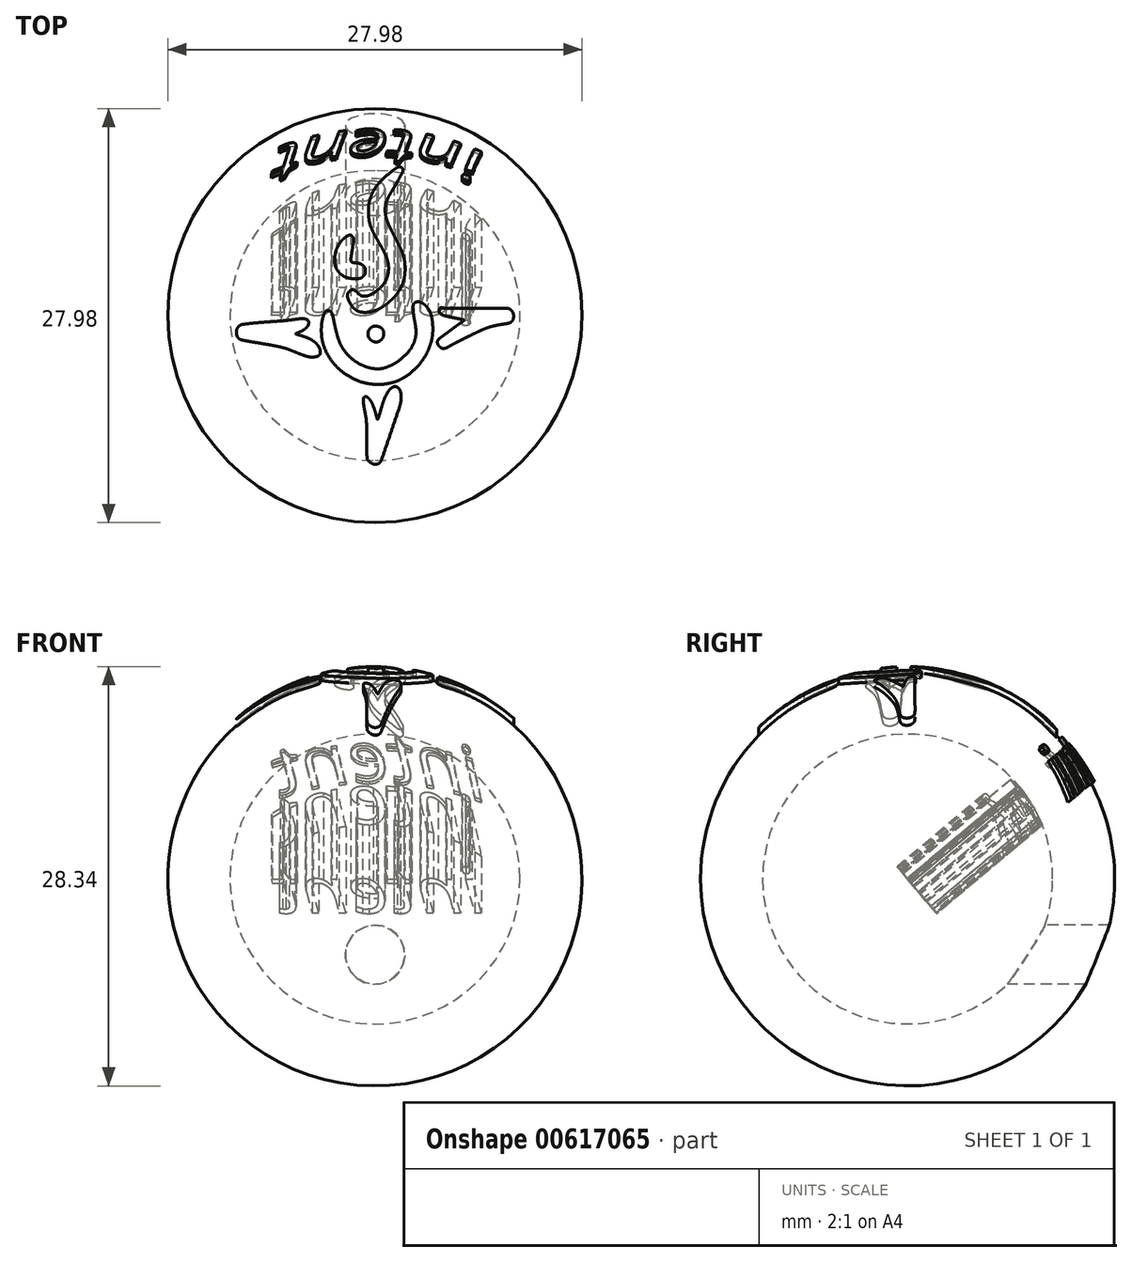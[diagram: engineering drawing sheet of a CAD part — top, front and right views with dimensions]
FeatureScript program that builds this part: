
annotation { "Feature Type Name" : "Feature", "Feature Type Description" : "" }
export const myFeature = defineFeature(function(context is Context, id is Id, definition is map)
    precondition{}
    {
        {
            var Q0;
            Q0=qCreatedBy(makeId("Top.planeOp"),FACE);
            var sketch = newSketch(context, id + "F0", { "sketchPlane" : qUnion([Q0])});
            skLineSegment(sketch, "E0", {"start": v(0, -10) * mm, "end": v(0, 10) * mm});
            skArc(sketch, "E1", {"start": v(0, 10) * mm, "mid": v(-10, 0) * mm, "end": v(0, -10) * mm});
            skSolve(sketch);
        }
        {
            var Q0;
            {var subQ0=sQuery(id+"F0.wireOp",EDGE,"E1");Q0=makeQuery(id+"F0.imprint","IMPRINT",FACE,{"disambiguationData":[TD([[makeQuery(id+"F0.imprint","IMPRINT",EDGE,{"derivedFrom":subQ0}),1.0]])]});}
            var Q1;
            Q1=sQuery(id+"F0.wireOp",EDGE,"E0");
            revolve(context, id + "F1", {"entities" : qUnion([Q0]), "axis" : qUnion([Q1]), "revolveType" : RevolveType.FULL});
        }
        {
            var Q0;
            Q0=makeQuery(id+"F1.opRevolve","SWEPT_BODY",BODY,{"disambiguationData":[OSD([sQuery(id+"F0.wireOp",EDGE,"E0"),sQuery(id+"F0.wireOp",EDGE,"E1")])]});
            var Q1;
            Q1=sQuery(id+"F0.wireOp",VERTEX,"NPe4G0ez-t7S9-9isL-QO5v-uuJu600mHcIT.center");
            var Q2;
            Q2=sQuery(id+"F0.wireOp",VERTEX,"E1.center");
            transform(context, id + "F2", {"entities" : qUnion([Q0]), "transformType" : TransformType.SCALE_UNIFORMLY, "scale" : 33.3, "scalePoint" : qUnion([Q2]), "makeCopy" : false});
        }
        {
            var Q0;
            Q0=qCreatedBy(makeId("Top.planeOp"),FACE);
            var sketch = newSketch(context, id + "F3", { "sketchPlane" : qUnion([Q0])});
            skArc(sketch, "E2", {"start": v(29.01, 233.55) * mm, "mid": v(19.13, 225.53) * mm, "end": v(9.84, 216.83) * mm});
            skArc(sketch, "E3", {"start": v(9.84, 216.83) * mm, "mid": v(3.12, 209.1) * mm, "end": v(-2.51, 200.54) * mm});
            skArc(sketch, "E4", {"start": v(-2.51, 200.54) * mm, "mid": v(-6.44, 192.13) * mm, "end": v(-9.04, 183.21) * mm});
            skArc(sketch, "E5", {"start": v(-9.04, 183.21) * mm, "mid": v(-10.44, 173.41) * mm, "end": v(-10.58, 163.51) * mm});
            skArc(sketch, "E6", {"start": v(-10.58, 163.51) * mm, "mid": v(-10.1, 157.75) * mm, "end": v(-9.24, 152.03) * mm});
            skArc(sketch, "E7", {"start": v(-9.24, 152.03) * mm, "mid": v(-8.07, 147.04) * mm, "end": v(-6.42, 142.18) * mm});
            skArc(sketch, "E8", {"start": v(-6.42, 142.18) * mm, "mid": v(-3.83, 136.15) * mm, "end": v(-0.88, 130.3) * mm});
            skArc(sketch, "E9", {"start": v(-0.88, 130.3) * mm, "mid": v(4.67, 120.25) * mm, "end": v(10.35, 110.28) * mm});
            skArc(sketch, "E10", {"start": v(10.35, 110.28) * mm, "mid": v(14.5, 102.5) * mm, "end": v(18.1, 94.45) * mm});
            skArc(sketch, "E11", {"start": v(18.1, 94.45) * mm, "mid": v(20.33, 87.78) * mm, "end": v(21.65, 80.87) * mm});
            skArc(sketch, "E12", {"start": v(21.65, 80.87) * mm, "mid": v(21.93, 74.62) * mm, "end": v(21.23, 68.4) * mm});
            skArc(sketch, "E13", {"start": v(21.23, 68.4) * mm, "mid": v(19.56, 62.07) * mm, "end": v(17.04, 56.03) * mm});
            skArc(sketch, "E14", {"start": v(17.04, 56.03) * mm, "mid": v(14.27, 51.34) * mm, "end": v(10.87, 47.1) * mm});
            skArc(sketch, "E15", {"start": v(10.87, 47.1) * mm, "mid": v(6.45, 42.75) * mm, "end": v(1.63, 38.84) * mm});
            skArc(sketch, "E16", {"start": v(1.63, 38.84) * mm, "mid": v(-3.27, 35.59) * mm, "end": v(-8.46, 32.84) * mm});
            skArc(sketch, "E17", {"start": v(-8.46, 32.84) * mm, "mid": v(-12.69, 31.4) * mm, "end": v(-17.12, 30.9) * mm});
            skArc(sketch, "E18", {"start": v(-17.12, 30.9) * mm, "mid": v(-18.57, 30.96) * mm, "end": v(-20.02, 31.11) * mm});
            skArc(sketch, "E19", {"start": v(-20.02, 31.11) * mm, "mid": v(-21.08, 31.35) * mm, "end": v(-22.08, 31.77) * mm});
            skArc(sketch, "E20", {"start": v(-22.08, 31.77) * mm, "mid": v(-23.2, 32.43) * mm, "end": v(-24.25, 33.22) * mm});
            skArc(sketch, "E21", {"start": v(-24.25, 33.22) * mm, "mid": v(-26.12, 34.84) * mm, "end": v(-27.96, 36.5) * mm});
            skArc(sketch, "E22", {"start": v(-27.96, 36.5) * mm, "mid": v(-29.65, 38.02) * mm, "end": v(-31.37, 39.52) * mm});
            skArc(sketch, "E23", {"start": v(-31.37, 39.52) * mm, "mid": v(-32.36, 40.29) * mm, "end": v(-33.42, 40.95) * mm});
            skArc(sketch, "E24", {"start": v(-33.42, 40.95) * mm, "mid": v(-34.2, 41.3) * mm, "end": v(-35.03, 41.5) * mm});
            skArc(sketch, "E25", {"start": v(-35.03, 41.5) * mm, "mid": v(-35.87, 41.54) * mm, "end": v(-36.7, 41.42) * mm});
            skArc(sketch, "E26", {"start": v(-36.7, 41.42) * mm, "mid": v(-38, 41) * mm, "end": v(-39.22, 40.4) * mm});
            skArc(sketch, "E27", {"start": v(-39.22, 40.4) * mm, "mid": v(-40.42, 39.6) * mm, "end": v(-41.52, 38.67) * mm});
            skArc(sketch, "E28", {"start": v(-41.52, 38.67) * mm, "mid": v(-42.45, 37.64) * mm, "end": v(-43.25, 36.51) * mm});
            skArc(sketch, "E29", {"start": v(-43.25, 36.51) * mm, "mid": v(-43.8, 35.42) * mm, "end": v(-44.14, 34.24) * mm});
            skArc(sketch, "E30", {"start": v(-44.14, 34.24) * mm, "mid": v(-44.33, 31.9) * mm, "end": v(-44.03, 29.59) * mm});
            skArc(sketch, "E31", {"start": v(-44.03, 29.59) * mm, "mid": v(-43.16, 26.53) * mm, "end": v(-42.02, 23.57) * mm});
            skArc(sketch, "E32", {"start": v(-42.02, 23.57) * mm, "mid": v(-40.5, 20.42) * mm, "end": v(-38.71, 17.4) * mm});
            skArc(sketch, "E33", {"start": v(-38.71, 17.4) * mm, "mid": v(-36.76, 14.69) * mm, "end": v(-34.56, 12.17) * mm});
            skArc(sketch, "E34", {"start": v(-34.56, 12.17) * mm, "mid": v(-32.5, 10.26) * mm, "end": v(-30.24, 8.58) * mm});
            skArc(sketch, "E35", {"start": v(-30.24, 8.58) * mm, "mid": v(-27.94, 7.28) * mm, "end": v(-25.49, 6.3) * mm});
            skArc(sketch, "E36", {"start": v(-25.49, 6.3) * mm, "mid": v(-22.72, 5.57) * mm, "end": v(-19.9, 5.18) * mm});
            skArc(sketch, "E37", {"start": v(-19.9, 5.18) * mm, "mid": v(-16.44, 5.03) * mm, "end": v(-12.99, 5.12) * mm});
            skArc(sketch, "E38", {"start": v(-12.99, 5.12) * mm, "mid": v(-7.73, 5.76) * mm, "end": v(-2.58, 7.01) * mm});
            skArc(sketch, "E39", {"start": v(-2.58, 7.01) * mm, "mid": v(2.77, 8.95) * mm, "end": v(7.9, 11.39) * mm});
            skArc(sketch, "E40", {"start": v(7.9, 11.39) * mm, "mid": v(13.3, 14.6) * mm, "end": v(18.4, 18.25) * mm});
            skArc(sketch, "E41", {"start": v(18.4, 18.25) * mm, "mid": v(23.75, 22.74) * mm, "end": v(28.83, 27.56) * mm});
            skArc(sketch, "E42", {"start": v(28.83, 27.56) * mm, "mid": v(33.48, 32.7) * mm, "end": v(37.66, 38.24) * mm});
            skArc(sketch, "E43", {"start": v(37.66, 38.24) * mm, "mid": v(41.04, 43.77) * mm, "end": v(43.8, 49.62) * mm});
            skArc(sketch, "E44", {"start": v(43.8, 49.62) * mm, "mid": v(45.9, 55.75) * mm, "end": v(47.34, 62.07) * mm});
            skArc(sketch, "E45", {"start": v(47.34, 62.07) * mm, "mid": v(48.2, 68.96) * mm, "end": v(48.46, 75.9) * mm});
            skArc(sketch, "E46", {"start": v(48.46, 75.9) * mm, "mid": v(48.28, 80.88) * mm, "end": v(47.83, 85.83) * mm});
            skArc(sketch, "E47", {"start": v(47.83, 85.83) * mm, "mid": v(47.14, 90.3) * mm, "end": v(46.11, 94.69) * mm});
            skArc(sketch, "E48", {"start": v(46.11, 94.69) * mm, "mid": v(44.7, 99.28) * mm, "end": v(42.96, 103.76) * mm});
            skArc(sketch, "E49", {"start": v(42.96, 103.76) * mm, "mid": v(40.56, 109.13) * mm, "end": v(37.96, 114.4) * mm});
            skArc(sketch, "E50", {"start": v(37.96, 114.4) * mm, "mid": v(32.65, 124.74) * mm, "end": v(27.37, 135.1) * mm});
            skArc(sketch, "E51", {"start": v(27.37, 135.1) * mm, "mid": v(24.73, 140.42) * mm, "end": v(22.2, 145.8) * mm});
            skArc(sketch, "E52", {"start": v(22.2, 145.8) * mm, "mid": v(20.66, 149.32) * mm, "end": v(19.27, 152.9) * mm});
            skArc(sketch, "E53", {"start": v(19.27, 152.9) * mm, "mid": v(18.3, 155.87) * mm, "end": v(17.54, 158.9) * mm});
            skArc(sketch, "E54", {"start": v(17.54, 158.9) * mm, "mid": v(16.72, 163.9) * mm, "end": v(16.36, 168.93) * mm});
            skArc(sketch, "E55", {"start": v(16.36, 168.93) * mm, "mid": v(16.52, 173.6) * mm, "end": v(17.22, 178.24) * mm});
            skArc(sketch, "E56", {"start": v(17.22, 178.24) * mm, "mid": v(18.5, 183.02) * mm, "end": v(20.27, 187.63) * mm});
            skArc(sketch, "E57", {"start": v(20.27, 187.63) * mm, "mid": v(22.83, 192.87) * mm, "end": v(25.73, 197.93) * mm});
            skArc(sketch, "E58", {"start": v(25.73, 197.93) * mm, "mid": v(28.95, 203.25) * mm, "end": v(32.1, 208.61) * mm});
            skArc(sketch, "E59", {"start": v(32.1, 208.61) * mm, "mid": v(35.38, 214.4) * mm, "end": v(38.59, 220.22) * mm});
            skArc(sketch, "E60", {"start": v(38.59, 220.22) * mm, "mid": v(41.58, 225.77) * mm, "end": v(44.55, 231.33) * mm});
            skArc(sketch, "E61", {"start": v(44.55, 231.33) * mm, "mid": v(45, 232.47) * mm, "end": v(45.14, 233.69) * mm});
            skArc(sketch, "E62", {"start": v(45.14, 233.69) * mm, "mid": v(45.05, 234.64) * mm, "end": v(44.77, 235.56) * mm});
            skArc(sketch, "E63", {"start": v(44.77, 235.56) * mm, "mid": v(44.32, 236.46) * mm, "end": v(43.72, 237.27) * mm});
            skArc(sketch, "E64", {"start": v(43.72, 237.27) * mm, "mid": v(42.97, 238) * mm, "end": v(42.1, 238.6) * mm});
            skArc(sketch, "E65", {"start": v(42.1, 238.6) * mm, "mid": v(41.14, 239.08) * mm, "end": v(40.11, 239.4) * mm});
            skArc(sketch, "E66", {"start": v(40.11, 239.4) * mm, "mid": v(39.26, 239.5) * mm, "end": v(38.42, 239.4) * mm});
            skArc(sketch, "E67", {"start": v(38.42, 239.4) * mm, "mid": v(37.38, 239.07) * mm, "end": v(36.4, 238.62) * mm});
            skArc(sketch, "E68", {"start": v(36.4, 238.62) * mm, "mid": v(34.96, 237.8) * mm, "end": v(33.58, 236.9) * mm});
            skArc(sketch, "E69", {"start": v(33.58, 236.9) * mm, "mid": v(31.29, 235.24) * mm, "end": v(29.01, 233.55) * mm});
            skArc(sketch, "E70", {"start": v(-45.92, 127.08) * mm, "mid": v(-50.13, 123.98) * mm, "end": v(-53.86, 120.31) * mm});
            skArc(sketch, "E71", {"start": v(-53.86, 120.31) * mm, "mid": v(-57.15, 116.09) * mm, "end": v(-59.87, 111.47) * mm});
            skArc(sketch, "E72", {"start": v(-59.87, 111.47) * mm, "mid": v(-62.06, 106.35) * mm, "end": v(-63.6, 101) * mm});
            skArc(sketch, "E73", {"start": v(-63.6, 101) * mm, "mid": v(-64.54, 95.27) * mm, "end": v(-64.85, 89.48) * mm});
            skArc(sketch, "E74", {"start": v(-64.85, 89.48) * mm, "mid": v(-64.72, 86.13) * mm, "end": v(-64.34, 82.8) * mm});
            skArc(sketch, "E75", {"start": v(-64.34, 82.8) * mm, "mid": v(-63.74, 79.95) * mm, "end": v(-62.82, 77.18) * mm});
            skArc(sketch, "E76", {"start": v(-62.82, 77.18) * mm, "mid": v(-61.64, 74.64) * mm, "end": v(-60.16, 72.26) * mm});
            skArc(sketch, "E77", {"start": v(-60.16, 72.26) * mm, "mid": v(-58.3, 69.89) * mm, "end": v(-56.23, 67.7) * mm});
            skArc(sketch, "E78", {"start": v(-56.23, 67.7) * mm, "mid": v(-54.01, 65.77) * mm, "end": v(-51.62, 64.06) * mm});
            skArc(sketch, "E79", {"start": v(-51.62, 64.06) * mm, "mid": v(-49.17, 62.64) * mm, "end": v(-46.6, 61.5) * mm});
            skArc(sketch, "E80", {"start": v(-46.6, 61.5) * mm, "mid": v(-43.73, 60.56) * mm, "end": v(-40.8, 59.9) * mm});
            skArc(sketch, "E81", {"start": v(-40.8, 59.9) * mm, "mid": v(-37.34, 59.42) * mm, "end": v(-33.86, 59.16) * mm});
            skArc(sketch, "E82", {"start": v(-33.86, 59.16) * mm, "mid": v(-30.5, 59.1) * mm, "end": v(-27.13, 59.26) * mm});
            skArc(sketch, "E83", {"start": v(-27.13, 59.26) * mm, "mid": v(-24.75, 59.62) * mm, "end": v(-22.46, 60.36) * mm});
            skArc(sketch, "E84", {"start": v(-22.46, 60.36) * mm, "mid": v(-20.66, 61.32) * mm, "end": v(-19.1, 62.63) * mm});
            skArc(sketch, "E85", {"start": v(-19.1, 62.63) * mm, "mid": v(-17.66, 64.36) * mm, "end": v(-16.5, 66.28) * mm});
            skArc(sketch, "E86", {"start": v(-16.5, 66.28) * mm, "mid": v(-15.4, 69.6) * mm, "end": v(-15.24, 73.08) * mm});
            skArc(sketch, "E87", {"start": v(-15.24, 73.08) * mm, "mid": v(-16.08, 76.33) * mm, "end": v(-17.88, 79.16) * mm});
            skArc(sketch, "E88", {"start": v(-17.88, 79.16) * mm, "mid": v(-20.75, 81.68) * mm, "end": v(-24.17, 83.38) * mm});
            skArc(sketch, "E89", {"start": v(-24.17, 83.38) * mm, "mid": v(-28.48, 84.49) * mm, "end": v(-32.91, 84.88) * mm});
            skArc(sketch, "E90", {"start": v(-32.91, 84.88) * mm, "mid": v(-34.86, 85.1) * mm, "end": v(-36.73, 85.7) * mm});
            skArc(sketch, "E91", {"start": v(-36.73, 85.7) * mm, "mid": v(-37.9, 86.6) * mm, "end": v(-38.52, 87.91) * mm});
            skArc(sketch, "E92", {"start": v(-38.52, 87.91) * mm, "mid": v(-38.8, 90.23) * mm, "end": v(-38.7, 92.56) * mm});
            skArc(sketch, "E93", {"start": v(-38.7, 92.56) * mm, "mid": v(-37.86, 98.3) * mm, "end": v(-36.95, 104.03) * mm});
            skArc(sketch, "E94", {"start": v(-36.95, 104.03) * mm, "mid": v(-35.78, 111.04) * mm, "end": v(-34.64, 118.06) * mm});
            skArc(sketch, "E95", {"start": v(-34.64, 118.06) * mm, "mid": v(-34.36, 120.3) * mm, "end": v(-34.22, 122.54) * mm});
            skArc(sketch, "E96", {"start": v(-34.22, 122.54) * mm, "mid": v(-34.32, 123.85) * mm, "end": v(-34.7, 125.11) * mm});
            skArc(sketch, "E97", {"start": v(-34.7, 125.11) * mm, "mid": v(-35.37, 126.33) * mm, "end": v(-36.26, 127.4) * mm});
            skArc(sketch, "E98", {"start": v(-36.26, 127.4) * mm, "mid": v(-37.31, 128.36) * mm, "end": v(-38.46, 129.21) * mm});
            skArc(sketch, "E99", {"start": v(-38.46, 129.21) * mm, "mid": v(-39.3, 129.61) * mm, "end": v(-40.24, 129.73) * mm});
            skArc(sketch, "E100", {"start": v(-40.24, 129.73) * mm, "mid": v(-41.31, 129.57) * mm, "end": v(-42.32, 129.17) * mm});
            skArc(sketch, "E101", {"start": v(-42.32, 129.17) * mm, "mid": v(-44.14, 128.16) * mm, "end": v(-45.92, 127.08) * mm});
            skArc(sketch, "E102", {"start": v(65.46, 21.4) * mm, "mid": v(64.85, 21.12) * mm, "end": v(64.26, 20.79) * mm});
            skArc(sketch, "E103", {"start": v(64.26, 20.79) * mm, "mid": v(63.68, 20.42) * mm, "end": v(63.13, 20) * mm});
            skArc(sketch, "E104", {"start": v(63.13, 20) * mm, "mid": v(62.68, 19.6) * mm, "end": v(62.25, 19.18) * mm});
            skArc(sketch, "E105", {"start": v(62.25, 19.18) * mm, "mid": v(61.98, 18.83) * mm, "end": v(61.79, 18.44) * mm});
            skArc(sketch, "E106", {"start": v(61.79, 18.44) * mm, "mid": v(61.29, 16.67) * mm, "end": v(61.1, 14.84) * mm});
            skArc(sketch, "E107", {"start": v(61.1, 14.84) * mm, "mid": v(61.15, 11.63) * mm, "end": v(61.3, 8.43) * mm});
            skArc(sketch, "E108", {"start": v(61.3, 8.43) * mm, "mid": v(61.65, 4.5) * mm, "end": v(62.14, 0.6) * mm});
            skArc(sketch, "E109", {"start": v(62.14, 0.6) * mm, "mid": v(62.82, -3.76) * mm, "end": v(63.62, -8.1) * mm});
            skArc(sketch, "E110", {"start": v(63.62, -8.1) * mm, "mid": v(64.53, -12.99) * mm, "end": v(65.32, -17.9) * mm});
            skArc(sketch, "E111", {"start": v(65.32, -17.9) * mm, "mid": v(65.76, -21.56) * mm, "end": v(65.99, -25.23) * mm});
            skArc(sketch, "E112", {"start": v(65.99, -25.23) * mm, "mid": v(65.98, -28.33) * mm, "end": v(65.74, -31.42) * mm});
            skArc(sketch, "E113", {"start": v(65.74, -31.42) * mm, "mid": v(65.29, -34.5) * mm, "end": v(64.6, -37.55) * mm});
            skArc(sketch, "E114", {"start": v(64.6, -37.55) * mm, "mid": v(61.01, -47.26) * mm, "end": v(55.57, -56.05) * mm});
            skArc(sketch, "E115", {"start": v(55.57, -56.05) * mm, "mid": v(47.83, -64.8) * mm, "end": v(38.95, -72.38) * mm});
            skArc(sketch, "E116", {"start": v(38.95, -72.38) * mm, "mid": v(29.3, -78.52) * mm, "end": v(18.86, -83.23) * mm});
            skArc(sketch, "E117", {"start": v(18.86, -83.23) * mm, "mid": v(9.39, -85.53) * mm, "end": v(-0.36, -85.64) * mm});
            skArc(sketch, "E118", {"start": v(-0.36, -85.64) * mm, "mid": v(-9.01, -84.12) * mm, "end": v(-17.37, -81.43) * mm});
            skArc(sketch, "E119", {"start": v(-17.37, -81.43) * mm, "mid": v(-25.6, -77.52) * mm, "end": v(-33.3, -72.63) * mm});
            skArc(sketch, "E120", {"start": v(-33.3, -72.63) * mm, "mid": v(-40.35, -66.8) * mm, "end": v(-46.63, -60.13) * mm});
            skArc(sketch, "E121", {"start": v(-46.63, -60.13) * mm, "mid": v(-51.86, -52.93) * mm, "end": v(-56.07, -45.1) * mm});
            skArc(sketch, "E122", {"start": v(-56.07, -45.1) * mm, "mid": v(-57.45, -41.85) * mm, "end": v(-58.65, -38.55) * mm});
            skArc(sketch, "E123", {"start": v(-58.65, -38.55) * mm, "mid": v(-59.98, -34.42) * mm, "end": v(-61.19, -30.25) * mm});
            skArc(sketch, "E124", {"start": v(-61.19, -30.25) * mm, "mid": v(-62.51, -25.22) * mm, "end": v(-63.72, -20.17) * mm});
            skArc(sketch, "E125", {"start": v(-63.72, -20.17) * mm, "mid": v(-65.05, -14.14) * mm, "end": v(-66.29, -8.1) * mm});
            skArc(sketch, "E126", {"start": v(-66.29, -8.1) * mm, "mid": v(-67.21, -3.72) * mm, "end": v(-68.25, 0.62) * mm});
            skArc(sketch, "E127", {"start": v(-68.25, 0.62) * mm, "mid": v(-68.99, 2.87) * mm, "end": v(-70.04, 4.98) * mm});
            skArc(sketch, "E128", {"start": v(-70.04, 4.98) * mm, "mid": v(-71.06, 6.23) * mm, "end": v(-72.4, 7.13) * mm});
            skArc(sketch, "E129", {"start": v(-72.4, 7.13) * mm, "mid": v(-74.06, 7.7) * mm, "end": v(-75.82, 7.9) * mm});
            skArc(sketch, "E130", {"start": v(-75.82, 7.9) * mm, "mid": v(-77.16, 7.74) * mm, "end": v(-78.43, 7.27) * mm});
            skArc(sketch, "E131", {"start": v(-78.43, 7.27) * mm, "mid": v(-79.54, 6.5) * mm, "end": v(-80.43, 5.5) * mm});
            skArc(sketch, "E132", {"start": v(-80.43, 5.5) * mm, "mid": v(-81.4, 3.84) * mm, "end": v(-82.13, 2.07) * mm});
            skArc(sketch, "E133", {"start": v(-82.13, 2.07) * mm, "mid": v(-83.1, -1) * mm, "end": v(-83.99, -4.1) * mm});
            skArc(sketch, "E134", {"start": v(-83.99, -4.1) * mm, "mid": v(-85.1, -9.01) * mm, "end": v(-85.83, -14) * mm});
            skArc(sketch, "E135", {"start": v(-85.83, -14) * mm, "mid": v(-86.25, -19.46) * mm, "end": v(-86.34, -24.93) * mm});
            skArc(sketch, "E136", {"start": v(-86.34, -24.93) * mm, "mid": v(-86.1, -30.38) * mm, "end": v(-85.54, -35.8) * mm});
            skArc(sketch, "E137", {"start": v(-85.54, -35.8) * mm, "mid": v(-84.67, -40.74) * mm, "end": v(-83.43, -45.6) * mm});
            skArc(sketch, "E138", {"start": v(-83.43, -45.6) * mm, "mid": v(-77.13, -61.14) * mm, "end": v(-68, -75.2) * mm});
            skArc(sketch, "E139", {"start": v(-68, -75.2) * mm, "mid": v(-56.22, -87.58) * mm, "end": v(-42.42, -97.64) * mm});
            skArc(sketch, "E140", {"start": v(-42.42, -97.64) * mm, "mid": v(-27.05, -105.06) * mm, "end": v(-10.6, -109.6) * mm});
            skArc(sketch, "E141", {"start": v(-10.6, -109.6) * mm, "mid": v(6.07, -111) * mm, "end": v(22.7, -109.2) * mm});
            skArc(sketch, "E142", {"start": v(22.7, -109.2) * mm, "mid": v(34.18, -105.87) * mm, "end": v(45, -100.8) * mm});
            skArc(sketch, "E143", {"start": v(45, -100.8) * mm, "mid": v(55.53, -93.83) * mm, "end": v(65.05, -85.53) * mm});
            skArc(sketch, "E144", {"start": v(65.05, -85.53) * mm, "mid": v(73.6, -75.81) * mm, "end": v(80.84, -65.07) * mm});
            skArc(sketch, "E145", {"start": v(80.84, -65.07) * mm, "mid": v(86.55, -53.59) * mm, "end": v(90.67, -41.45) * mm});
            skArc(sketch, "E146", {"start": v(90.67, -41.45) * mm, "mid": v(91.87, -36) * mm, "end": v(92.6, -30.49) * mm});
            skArc(sketch, "E147", {"start": v(92.6, -30.49) * mm, "mid": v(92.96, -24.25) * mm, "end": v(92.94, -18) * mm});
            skArc(sketch, "E148", {"start": v(92.94, -18) * mm, "mid": v(92.53, -11.87) * mm, "end": v(91.75, -5.78) * mm});
            skArc(sketch, "E149", {"start": v(91.75, -5.78) * mm, "mid": v(90.67, -0.67) * mm, "end": v(89.09, 4.31) * mm});
            skArc(sketch, "E150", {"start": v(89.09, 4.31) * mm, "mid": v(87.2, 8.44) * mm, "end": v(84.75, 12.25) * mm});
            skArc(sketch, "E151", {"start": v(84.75, 12.25) * mm, "mid": v(81.83, 15.6) * mm, "end": v(78.44, 18.46) * mm});
            skArc(sketch, "E152", {"start": v(78.44, 18.46) * mm, "mid": v(75.14, 20.43) * mm, "end": v(71.54, 21.78) * mm});
            skArc(sketch, "E153", {"start": v(71.54, 21.78) * mm, "mid": v(68.47, 22.1) * mm, "end": v(65.46, 21.4) * mm});
            skArc(sketch, "E154", {"start": v(103.85, 10.27) * mm, "mid": v(103.2, 8.18) * mm, "end": v(103.3, 5.98) * mm});
            skArc(sketch, "E155", {"start": v(103.3, 5.98) * mm, "mid": v(104.13, 4.02) * mm, "end": v(105.62, 2.5) * mm});
            skArc(sketch, "E156", {"start": v(105.62, 2.5) * mm, "mid": v(108.58, 0.82) * mm, "end": v(111.77, -0.35) * mm});
            skArc(sketch, "E157", {"start": v(111.77, -0.35) * mm, "mid": v(117.43, -1.78) * mm, "end": v(123.14, -3) * mm});
            skArc(sketch, "E158", {"start": v(123.14, -3) * mm, "mid": v(125.34, -3.44) * mm, "end": v(127.55, -3.88) * mm});
            skArc(sketch, "E159", {"start": v(127.55, -3.88) * mm, "mid": v(129.83, -4.33) * mm, "end": v(132.11, -4.78) * mm});
            skArc(sketch, "E160", {"start": v(132.11, -4.78) * mm, "mid": v(134.16, -5.19) * mm, "end": v(136.2, -5.6) * mm});
            skArc(sketch, "E161", {"start": v(136.2, -5.6) * mm, "mid": v(137.57, -5.88) * mm, "end": v(138.94, -6.16) * mm});
            skLineSegment(sketch, "E162", {"start": v(138.94, -6.16) * mm, "end": v(144.24, -7.26) * mm});
            skLineSegment(sketch, "E163", {"start": v(144.24, -7.26) * mm, "end": v(138.6, -11.21) * mm});
            skArc(sketch, "E164", {"start": v(138.6, -11.21) * mm, "mid": v(137.18, -12.21) * mm, "end": v(135.77, -13.23) * mm});
            skArc(sketch, "E165", {"start": v(135.77, -13.23) * mm, "mid": v(133.77, -14.68) * mm, "end": v(131.77, -16.14) * mm});
            skArc(sketch, "E166", {"start": v(131.77, -16.14) * mm, "mid": v(129.58, -17.75) * mm, "end": v(127.4, -19.37) * mm});
            skArc(sketch, "E167", {"start": v(127.4, -19.37) * mm, "mid": v(125.35, -20.9) * mm, "end": v(123.3, -22.45) * mm});
            skArc(sketch, "E168", {"start": v(123.3, -22.45) * mm, "mid": v(121.22, -24) * mm, "end": v(119.15, -25.54) * mm});
            skArc(sketch, "E169", {"start": v(119.15, -25.54) * mm, "mid": v(116.91, -27.18) * mm, "end": v(114.67, -28.8) * mm});
            skArc(sketch, "E170", {"start": v(114.67, -28.8) * mm, "mid": v(112.6, -30.3) * mm, "end": v(110.53, -31.78) * mm});
            skArc(sketch, "E171", {"start": v(110.53, -31.78) * mm, "mid": v(109.02, -32.83) * mm, "end": v(107.5, -33.87) * mm});
            skArc(sketch, "E172", {"start": v(107.5, -33.87) * mm, "mid": v(104.91, -35.81) * mm, "end": v(102.52, -38) * mm});
            skArc(sketch, "E173", {"start": v(102.52, -38) * mm, "mid": v(101.18, -39.8) * mm, "end": v(100.4, -41.9) * mm});
            skArc(sketch, "E174", {"start": v(100.4, -41.9) * mm, "mid": v(100.3, -43.94) * mm, "end": v(100.88, -45.9) * mm});
            skArc(sketch, "E175", {"start": v(100.88, -45.9) * mm, "mid": v(102.25, -48.24) * mm, "end": v(103.94, -50.34) * mm});
            skArc(sketch, "E176", {"start": v(103.94, -50.34) * mm, "mid": v(105.3, -51.53) * mm, "end": v(106.85, -52.43) * mm});
            skArc(sketch, "E177", {"start": v(106.85, -52.43) * mm, "mid": v(108.5, -52.96) * mm, "end": v(110.22, -53.1) * mm});
            skArc(sketch, "E178", {"start": v(110.22, -53.1) * mm, "mid": v(112.2, -52.89) * mm, "end": v(114.12, -52.31) * mm});
            skArc(sketch, "E179", {"start": v(114.12, -52.31) * mm, "mid": v(116.4, -51.27) * mm, "end": v(118.59, -50.02) * mm});
            skArc(sketch, "E180", {"start": v(118.59, -50.02) * mm, "mid": v(120.15, -49.08) * mm, "end": v(121.76, -48.19) * mm});
            skArc(sketch, "E181", {"start": v(121.76, -48.19) * mm, "mid": v(125.82, -46.06) * mm, "end": v(129.89, -43.95) * mm});
            skArc(sketch, "E182", {"start": v(129.89, -43.95) * mm, "mid": v(134.76, -41.44) * mm, "end": v(139.64, -38.96) * mm});
            skArc(sketch, "E183", {"start": v(139.64, -38.96) * mm, "mid": v(144.95, -36.29) * mm, "end": v(150.27, -33.64) * mm});
            skArc(sketch, "E184", {"start": v(150.27, -33.64) * mm, "mid": v(159.77, -29) * mm, "end": v(169.33, -24.46) * mm});
            skArc(sketch, "E185", {"start": v(169.33, -24.46) * mm, "mid": v(175.2, -21.89) * mm, "end": v(181.2, -19.6) * mm});
            skArc(sketch, "E186", {"start": v(181.2, -19.6) * mm, "mid": v(186.48, -17.91) * mm, "end": v(191.84, -16.56) * mm});
            skArc(sketch, "E187", {"start": v(191.84, -16.56) * mm, "mid": v(198.67, -15.2) * mm, "end": v(205.54, -14.04) * mm});
            skArc(sketch, "E188", {"start": v(205.54, -14.04) * mm, "mid": v(208.79, -13.53) * mm, "end": v(212.03, -12.98) * mm});
            skArc(sketch, "E189", {"start": v(212.03, -12.98) * mm, "mid": v(213.87, -12.6) * mm, "end": v(215.7, -12.11) * mm});
            skArc(sketch, "E190", {"start": v(215.7, -12.11) * mm, "mid": v(216.92, -11.68) * mm, "end": v(218.09, -11.13) * mm});
            skArc(sketch, "E191", {"start": v(218.09, -11.13) * mm, "mid": v(219.06, -10.5) * mm, "end": v(219.93, -9.76) * mm});
            skArc(sketch, "E192", {"start": v(219.93, -9.76) * mm, "mid": v(221.11, -8.3) * mm, "end": v(221.97, -6.62) * mm});
            skArc(sketch, "E193", {"start": v(221.97, -6.62) * mm, "mid": v(222.6, -4.57) * mm, "end": v(222.93, -2.44) * mm});
            skArc(sketch, "E194", {"start": v(222.93, -2.44) * mm, "mid": v(222.96, -0.25) * mm, "end": v(222.7, 1.92) * mm});
            skArc(sketch, "E195", {"start": v(222.7, 1.92) * mm, "mid": v(222.14, 3.83) * mm, "end": v(221.24, 5.6) * mm});
            skArc(sketch, "E196", {"start": v(221.24, 5.6) * mm, "mid": v(219.73, 7.65) * mm, "end": v(217.92, 9.44) * mm});
            skArc(sketch, "E197", {"start": v(217.92, 9.44) * mm, "mid": v(216.13, 10.6) * mm, "end": v(214.1, 11.29) * mm});
            skArc(sketch, "E198", {"start": v(214.1, 11.29) * mm, "mid": v(210.86, 11.76) * mm, "end": v(207.59, 11.92) * mm});
            skArc(sketch, "E199", {"start": v(207.59, 11.92) * mm, "mid": v(198.73, 11.88) * mm, "end": v(189.88, 11.78) * mm});
            skArc(sketch, "E200", {"start": v(189.88, 11.78) * mm, "mid": v(175.63, 11.6) * mm, "end": v(161.38, 11.47) * mm});
            skArc(sketch, "E201", {"start": v(161.38, 11.47) * mm, "mid": v(148.64, 11.43) * mm, "end": v(135.9, 11.47) * mm});
            skArc(sketch, "E202", {"start": v(135.9, 11.47) * mm, "mid": v(125.01, 11.56) * mm, "end": v(114.12, 11.68) * mm});
            skArc(sketch, "E203", {"start": v(114.12, 11.68) * mm, "mid": v(111.53, 11.85) * mm, "end": v(108.98, 12.3) * mm});
            skArc(sketch, "E204", {"start": v(108.98, 12.3) * mm, "mid": v(107.88, 12.53) * mm, "end": v(106.78, 12.7) * mm});
            skArc(sketch, "E205", {"start": v(106.78, 12.7) * mm, "mid": v(106.2, 12.72) * mm, "end": v(105.65, 12.58) * mm});
            skArc(sketch, "E206", {"start": v(105.65, 12.58) * mm, "mid": v(105.18, 12.3) * mm, "end": v(104.81, 11.9) * mm});
            skArc(sketch, "E207", {"start": v(104.81, 11.9) * mm, "mid": v(104.3, 11.1) * mm, "end": v(103.85, 10.27) * mm});
            skArc(sketch, "E208", {"start": v(-131.36, -6.65) * mm, "mid": v(-133.6, -7) * mm, "end": v(-135.83, -7.27) * mm});
            skArc(sketch, "E209", {"start": v(-135.83, -7.27) * mm, "mid": v(-139.72, -7.68) * mm, "end": v(-143.62, -8.06) * mm});
            skArc(sketch, "E210", {"start": v(-143.62, -8.06) * mm, "mid": v(-148.14, -8.47) * mm, "end": v(-152.66, -8.86) * mm});
            skArc(sketch, "E211", {"start": v(-152.66, -8.86) * mm, "mid": v(-157.26, -9.22) * mm, "end": v(-161.86, -9.55) * mm});
            skArc(sketch, "E212", {"start": v(-161.86, -9.55) * mm, "mid": v(-173.2, -10.37) * mm, "end": v(-184.55, -11.25) * mm});
            skArc(sketch, "E213", {"start": v(-184.55, -11.25) * mm, "mid": v(-192.69, -11.96) * mm, "end": v(-200.81, -12.79) * mm});
            skArc(sketch, "E214", {"start": v(-200.81, -12.79) * mm, "mid": v(-206.72, -13.48) * mm, "end": v(-212.61, -14.24) * mm});
            skArc(sketch, "E215", {"start": v(-212.61, -14.24) * mm, "mid": v(-214.78, -14.73) * mm, "end": v(-216.83, -15.58) * mm});
            skArc(sketch, "E216", {"start": v(-216.83, -15.58) * mm, "mid": v(-219.48, -17.53) * mm, "end": v(-221.38, -20.22) * mm});
            skArc(sketch, "E217", {"start": v(-221.38, -20.22) * mm, "mid": v(-222.6, -23.66) * mm, "end": v(-222.98, -27.29) * mm});
            skArc(sketch, "E218", {"start": v(-222.98, -27.29) * mm, "mid": v(-222.51, -30.87) * mm, "end": v(-221.21, -34.25) * mm});
            skArc(sketch, "E219", {"start": v(-221.21, -34.25) * mm, "mid": v(-219.25, -36.82) * mm, "end": v(-216.57, -38.61) * mm});
            skArc(sketch, "E220", {"start": v(-216.57, -38.61) * mm, "mid": v(-215.48, -39.03) * mm, "end": v(-214.35, -39.34) * mm});
            skArc(sketch, "E221", {"start": v(-214.35, -39.34) * mm, "mid": v(-211.03, -40.03) * mm, "end": v(-207.7, -40.7) * mm});
            skArc(sketch, "E222", {"start": v(-207.7, -40.7) * mm, "mid": v(-203.7, -41.46) * mm, "end": v(-199.71, -42.18) * mm});
            skArc(sketch, "E223", {"start": v(-199.71, -42.18) * mm, "mid": v(-195.29, -42.94) * mm, "end": v(-190.86, -43.67) * mm});
            skArc(sketch, "E224", {"start": v(-190.86, -43.67) * mm, "mid": v(-179.98, -45.46) * mm, "end": v(-169.1, -47.31) * mm});
            skArc(sketch, "E225", {"start": v(-169.1, -47.31) * mm, "mid": v(-161.88, -48.66) * mm, "end": v(-154.68, -50.16) * mm});
            skArc(sketch, "E226", {"start": v(-154.68, -50.16) * mm, "mid": v(-149.45, -51.4) * mm, "end": v(-144.25, -52.8) * mm});
            skArc(sketch, "E227", {"start": v(-144.25, -52.8) * mm, "mid": v(-140.08, -54.14) * mm, "end": v(-135.99, -55.72) * mm});
            skArc(sketch, "E228", {"start": v(-135.99, -55.72) * mm, "mid": v(-130.47, -58) * mm, "end": v(-124.93, -60.26) * mm});
            skArc(sketch, "E229", {"start": v(-124.93, -60.26) * mm, "mid": v(-120.71, -61.9) * mm, "end": v(-116.47, -63.47) * mm});
            skArc(sketch, "E230", {"start": v(-116.47, -63.47) * mm, "mid": v(-113.25, -64.59) * mm, "end": v(-110, -65.63) * mm});
            skArc(sketch, "E231", {"start": v(-110, -65.63) * mm, "mid": v(-107.83, -66.2) * mm, "end": v(-105.61, -66.62) * mm});
            skArc(sketch, "E232", {"start": v(-105.61, -66.62) * mm, "mid": v(-103.25, -66.88) * mm, "end": v(-100.88, -66.95) * mm});
            skArc(sketch, "E233", {"start": v(-100.88, -66.95) * mm, "mid": v(-98.54, -66.85) * mm, "end": v(-96.2, -66.56) * mm});
            skArc(sketch, "E234", {"start": v(-96.2, -66.56) * mm, "mid": v(-94.2, -66.14) * mm, "end": v(-92.24, -65.56) * mm});
            skArc(sketch, "E235", {"start": v(-92.24, -65.56) * mm, "mid": v(-90.93, -64.93) * mm, "end": v(-89.79, -64.02) * mm});
            skArc(sketch, "E236", {"start": v(-89.79, -64.02) * mm, "mid": v(-88.55, -62.26) * mm, "end": v(-88, -60.17) * mm});
            skArc(sketch, "E237", {"start": v(-88, -60.17) * mm, "mid": v(-88.02, -57.48) * mm, "end": v(-88.54, -54.84) * mm});
            skArc(sketch, "E238", {"start": v(-88.54, -54.84) * mm, "mid": v(-89.66, -51.83) * mm, "end": v(-91.23, -49.03) * mm});
            skArc(sketch, "E239", {"start": v(-91.23, -49.03) * mm, "mid": v(-93.28, -46.32) * mm, "end": v(-95.66, -43.89) * mm});
            skArc(sketch, "E240", {"start": v(-95.66, -43.89) * mm, "mid": v(-97.72, -42.15) * mm, "end": v(-99.9, -40.55) * mm});
            skArc(sketch, "E241", {"start": v(-99.9, -40.55) * mm, "mid": v(-102.15, -39.12) * mm, "end": v(-104.5, -37.84) * mm});
            skArc(sketch, "E242", {"start": v(-104.5, -37.84) * mm, "mid": v(-107.34, -36.51) * mm, "end": v(-110.26, -35.34) * mm});
            skArc(sketch, "E243", {"start": v(-110.26, -35.34) * mm, "mid": v(-114.24, -33.92) * mm, "end": v(-118.25, -32.59) * mm});
            skLineSegment(sketch, "E244", {"start": v(-118.25, -32.59) * mm, "end": v(-128.14, -29.44) * mm});
            skLineSegment(sketch, "E245", {"start": v(-128.14, -29.44) * mm, "end": v(-122.48, -27.14) * mm});
            skArc(sketch, "E246", {"start": v(-122.48, -27.14) * mm, "mid": v(-119.78, -25.96) * mm, "end": v(-117.15, -24.64) * mm});
            skArc(sketch, "E247", {"start": v(-117.15, -24.64) * mm, "mid": v(-114.93, -23.33) * mm, "end": v(-112.83, -21.85) * mm});
            skArc(sketch, "E248", {"start": v(-112.83, -21.85) * mm, "mid": v(-111.13, -20.42) * mm, "end": v(-109.57, -18.83) * mm});
            skArc(sketch, "E249", {"start": v(-109.57, -18.83) * mm, "mid": v(-108.4, -17.3) * mm, "end": v(-107.44, -15.62) * mm});
            skArc(sketch, "E250", {"start": v(-107.44, -15.62) * mm, "mid": v(-106.65, -12.83) * mm, "end": v(-106.8, -9.93) * mm});
            skArc(sketch, "E251", {"start": v(-106.8, -9.93) * mm, "mid": v(-107.92, -7.7) * mm, "end": v(-109.97, -6.27) * mm});
            skArc(sketch, "E252", {"start": v(-109.97, -6.27) * mm, "mid": v(-113.9, -5.25) * mm, "end": v(-117.95, -5.09) * mm});
            skArc(sketch, "E253", {"start": v(-117.95, -5.09) * mm, "mid": v(-124.68, -5.7) * mm, "end": v(-131.36, -6.65) * mm});
            skArc(sketch, "E254", {"start": v(-6.77, -19.67) * mm, "mid": v(-9.2, -22.4) * mm, "end": v(-10.77, -25.7) * mm});
            skArc(sketch, "E255", {"start": v(-10.77, -25.7) * mm, "mid": v(-11.35, -29.33) * mm, "end": v(-10.89, -32.97) * mm});
            skArc(sketch, "E256", {"start": v(-10.89, -32.97) * mm, "mid": v(-9.42, -36.37) * mm, "end": v(-7.06, -39.22) * mm});
            skArc(sketch, "E257", {"start": v(-7.06, -39.22) * mm, "mid": v(-4, -41.32) * mm, "end": v(-0.49, -42.5) * mm});
            skArc(sketch, "E258", {"start": v(-0.49, -42.5) * mm, "mid": v(2.99, -42.62) * mm, "end": v(6.33, -41.7) * mm});
            skArc(sketch, "E259", {"start": v(6.33, -41.7) * mm, "mid": v(9.37, -39.8) * mm, "end": v(11.78, -37.15) * mm});
            skArc(sketch, "E260", {"start": v(11.78, -37.15) * mm, "mid": v(13.43, -33.86) * mm, "end": v(14.16, -30.26) * mm});
            skArc(sketch, "E261", {"start": v(14.16, -30.26) * mm, "mid": v(13.9, -26.62) * mm, "end": v(12.68, -23.18) * mm});
            skArc(sketch, "E262", {"start": v(12.68, -23.18) * mm, "mid": v(11.21, -21.09) * mm, "end": v(9.23, -19.47) * mm});
            skArc(sketch, "E263", {"start": v(9.23, -19.47) * mm, "mid": v(6.62, -18.2) * mm, "end": v(3.8, -17.4) * mm});
            skArc(sketch, "E264", {"start": v(3.8, -17.4) * mm, "mid": v(0.87, -17.15) * mm, "end": v(-2.06, -17.43) * mm});
            skArc(sketch, "E265", {"start": v(-2.06, -17.43) * mm, "mid": v(-4.56, -18.25) * mm, "end": v(-6.77, -19.67) * mm});
            skArc(sketch, "E266", {"start": v(27.49, -116.02) * mm, "mid": v(24.94, -117.92) * mm, "end": v(22.78, -120.24) * mm});
            skArc(sketch, "E267", {"start": v(22.78, -120.24) * mm, "mid": v(20.4, -123.6) * mm, "end": v(18.33, -127.14) * mm});
            skArc(sketch, "E268", {"start": v(18.33, -127.14) * mm, "mid": v(16.08, -131.78) * mm, "end": v(14.16, -136.56) * mm});
            skArc(sketch, "E269", {"start": v(14.16, -136.56) * mm, "mid": v(12.1, -142.55) * mm, "end": v(10.27, -148.62) * mm});
            skArc(sketch, "E270", {"start": v(10.27, -148.62) * mm, "mid": v(8.7, -154.13) * mm, "end": v(7.12, -159.63) * mm});
            skArc(sketch, "E271", {"start": v(7.12, -159.63) * mm, "mid": v(6.33, -162.23) * mm, "end": v(5.48, -164.8) * mm});
            skArc(sketch, "E272", {"start": v(5.48, -164.8) * mm, "mid": v(5.01, -166) * mm, "end": v(4.46, -167.15) * mm});
            skArc(sketch, "E273", {"start": v(4.46, -167.15) * mm, "mid": v(4.15, -167.32) * mm, "end": v(3.87, -167.1) * mm});
            skArc(sketch, "E274", {"start": v(3.87, -167.1) * mm, "mid": v(3.71, -166.6) * mm, "end": v(3.56, -166.1) * mm});
            skArc(sketch, "E275", {"start": v(3.56, -166.1) * mm, "mid": v(3.15, -164.68) * mm, "end": v(2.74, -163.27) * mm});
            skArc(sketch, "E276", {"start": v(2.74, -163.27) * mm, "mid": v(2.25, -161.58) * mm, "end": v(1.76, -159.89) * mm});
            skArc(sketch, "E277", {"start": v(1.76, -159.89) * mm, "mid": v(1.23, -158.03) * mm, "end": v(0.7, -156.17) * mm});
            skArc(sketch, "E278", {"start": v(0.7, -156.17) * mm, "mid": v(-1.17, -150.27) * mm, "end": v(-3.35, -144.48) * mm});
            skArc(sketch, "E279", {"start": v(-3.35, -144.48) * mm, "mid": v(-5.42, -140.1) * mm, "end": v(-7.98, -135.98) * mm});
            skArc(sketch, "E280", {"start": v(-7.98, -135.98) * mm, "mid": v(-10.1, -133.45) * mm, "end": v(-12.64, -131.33) * mm});
            skArc(sketch, "E281", {"start": v(-12.64, -131.33) * mm, "mid": v(-14.72, -130.62) * mm, "end": v(-16.86, -131.1) * mm});
            skArc(sketch, "E282", {"start": v(-16.86, -131.1) * mm, "mid": v(-17.88, -131.97) * mm, "end": v(-18.44, -133.2) * mm});
            skArc(sketch, "E283", {"start": v(-18.44, -133.2) * mm, "mid": v(-18.75, -135.34) * mm, "end": v(-18.81, -137.5) * mm});
            skArc(sketch, "E284", {"start": v(-18.81, -137.5) * mm, "mid": v(-18.6, -140.93) * mm, "end": v(-18.15, -144.33) * mm});
            skArc(sketch, "E285", {"start": v(-18.15, -144.33) * mm, "mid": v(-17.2, -149.77) * mm, "end": v(-16.15, -155.19) * mm});
            skArc(sketch, "E286", {"start": v(-16.15, -155.19) * mm, "mid": v(-15.31, -159.57) * mm, "end": v(-14.58, -163.98) * mm});
            skArc(sketch, "E287", {"start": v(-14.58, -163.98) * mm, "mid": v(-14.12, -167.49) * mm, "end": v(-13.82, -171.02) * mm});
            skArc(sketch, "E288", {"start": v(-13.82, -171.02) * mm, "mid": v(-13.6, -175.56) * mm, "end": v(-13.5, -180.1) * mm});
            skArc(sketch, "E289", {"start": v(-13.5, -180.1) * mm, "mid": v(-13.43, -189.6) * mm, "end": v(-13.4, -199.1) * mm});
            skArc(sketch, "E290", {"start": v(-13.4, -199.1) * mm, "mid": v(-13.37, -206.13) * mm, "end": v(-13.32, -213.17) * mm});
            skArc(sketch, "E291", {"start": v(-13.32, -213.17) * mm, "mid": v(-13.24, -217.98) * mm, "end": v(-13.1, -222.78) * mm});
            skArc(sketch, "E292", {"start": v(-13.1, -222.78) * mm, "mid": v(-12.95, -226.25) * mm, "end": v(-12.77, -229.7) * mm});
            skArc(sketch, "E293", {"start": v(-12.77, -229.7) * mm, "mid": v(-12.6, -230.68) * mm, "end": v(-12.2, -231.6) * mm});
            skArc(sketch, "E294", {"start": v(-12.2, -231.6) * mm, "mid": v(-11.4, -232.81) * mm, "end": v(-10.49, -233.94) * mm});
            skArc(sketch, "E295", {"start": v(-10.49, -233.94) * mm, "mid": v(-9.39, -235.05) * mm, "end": v(-8.2, -236.07) * mm});
            skArc(sketch, "E296", {"start": v(-8.2, -236.07) * mm, "mid": v(-6.9, -237) * mm, "end": v(-5.53, -237.81) * mm});
            skArc(sketch, "E297", {"start": v(-5.53, -237.81) * mm, "mid": v(-4.14, -238.48) * mm, "end": v(-2.7, -239.02) * mm});
            skArc(sketch, "E298", {"start": v(-2.7, -239.02) * mm, "mid": v(-1.05, -239.4) * mm, "end": v(0.64, -239.5) * mm});
            skArc(sketch, "E299", {"start": v(0.64, -239.5) * mm, "mid": v(2.4, -239.33) * mm, "end": v(4.13, -238.91) * mm});
            skArc(sketch, "E300", {"start": v(4.13, -238.91) * mm, "mid": v(5.7, -238.27) * mm, "end": v(7.14, -237.4) * mm});
            skArc(sketch, "E301", {"start": v(7.14, -237.4) * mm, "mid": v(8.23, -236.44) * mm, "end": v(9.06, -235.24) * mm});
            skArc(sketch, "E302", {"start": v(9.06, -235.24) * mm, "mid": v(10.25, -232.78) * mm, "end": v(11.23, -230.24) * mm});
            skArc(sketch, "E303", {"start": v(11.23, -230.24) * mm, "mid": v(18.28, -209.56) * mm, "end": v(25.31, -188.88) * mm});
            skArc(sketch, "E304", {"start": v(25.31, -188.88) * mm, "mid": v(32.2, -168.57) * mm, "end": v(39.07, -148.26) * mm});
            skArc(sketch, "E305", {"start": v(39.07, -148.26) * mm, "mid": v(40.17, -144.7) * mm, "end": v(41.05, -141.07) * mm});
            skArc(sketch, "E306", {"start": v(41.05, -141.07) * mm, "mid": v(41.76, -136.98) * mm, "end": v(42.13, -132.84) * mm});
            skArc(sketch, "E307", {"start": v(42.13, -132.84) * mm, "mid": v(42.1, -129.09) * mm, "end": v(41.67, -125.36) * mm});
            skArc(sketch, "E308", {"start": v(41.67, -125.36) * mm, "mid": v(40.95, -122.35) * mm, "end": v(39.84, -119.46) * mm});
            skArc(sketch, "E309", {"start": v(39.84, -119.46) * mm, "mid": v(38.55, -117.5) * mm, "end": v(36.74, -116) * mm});
            skArc(sketch, "E310", {"start": v(36.74, -116) * mm, "mid": v(35.45, -115.26) * mm, "end": v(34.1, -114.62) * mm});
            skArc(sketch, "E311", {"start": v(34.1, -114.62) * mm, "mid": v(33.14, -114.32) * mm, "end": v(32.13, -114.22) * mm});
            skArc(sketch, "E312", {"start": v(32.13, -114.22) * mm, "mid": v(31.12, -114.32) * mm, "end": v(30.15, -114.64) * mm});
            skArc(sketch, "E313", {"start": v(30.15, -114.64) * mm, "mid": v(28.8, -115.28) * mm, "end": v(27.49, -116.02) * mm});
            skSolve(sketch);
        }
        {
            var Q0;
            Q0=qSketchRegion(id+"F3",true);
            var Q1;
            Q1=sQuery(id+"F3.wireOp",EDGE,"c928f899-12af-4b01-b412-b3b7da3d830f");
            var Q2;
            Q2=sQuery(id+"F3.wireOp",EDGE,"b69f99c7-a6d0-4d1b-8752-9e82ab4c99ec");
            extrude(context, id + "F4", {"entities" : qUnion([Q0]), "operationType" : NewBodyOperationType.ADD, "surfaceEntities" : qUnion([Q1, Q2]), "depth" : 350 * mm});
        }
        {
            var Q0;
            Q0=makeQuery(id+"F4.opExtrude","SWEPT_BODY",BODY,{"disambiguationData":[OSD([sQuery(id+"F3.wireOp",EDGE,"15c6da4e-992d-4824-9d20-70d2d6be9970"),sQuery(id+"F3.wireOp",EDGE,"268c69ec-46be-456f-85eb-69decc32fe39"),sQuery(id+"F3.wireOp",EDGE,"1d386307-6059-4203-bca6-0c1cec3c82e1"),sQuery(id+"F3.wireOp",EDGE,"7d7c66d2-f869-427f-806b-ad436cacd60e"),sQuery(id+"F3.wireOp",EDGE,"1db91850-860e-493f-a3af-7a0f3f1512ae"),sQuery(id+"F3.wireOp",EDGE,"2c65f23b-9f03-4f6f-ab37-de452af29e3c"),sQuery(id+"F3.wireOp",EDGE,"ba006cbc-bbd7-44d9-84cc-9cde0967c280"),sQuery(id+"F3.wireOp",EDGE,"ae950208-c781-4a25-8fcf-ffe59b9085ff"),sQuery(id+"F3.wireOp",EDGE,"3cce0944-c62d-4831-9b9d-d1a418d328b4"),sQuery(id+"F3.wireOp",EDGE,"9edc5e7d-16c0-40c4-98ad-6b91d5df0e78"),sQuery(id+"F3.wireOp",EDGE,"aa452f44-44a2-4c64-bff5-a2a639df00db"),sQuery(id+"F3.wireOp",EDGE,"16259f99-ce20-4b7b-81e1-fa0909c03eb4"),sQuery(id+"F3.wireOp",EDGE,"79895566-a943-429d-b257-d76af3645bdf"),sQuery(id+"F3.wireOp",EDGE,"a85490ef-f17e-45c8-b92b-28215162778a"),sQuery(id+"F3.wireOp",EDGE,"322f1036-a6fd-4992-ab69-5919540af7a6"),sQuery(id+"F3.wireOp",EDGE,"0a87ff38-4ab4-4140-b3c3-2d7501d9f3b1"),sQuery(id+"F3.wireOp",EDGE,"a6e7bdf2-ef3e-49d4-9b3c-e34f5a41e0c4"),sQuery(id+"F3.wireOp",EDGE,"3e588790-576f-47c1-9730-f5e27fa1e8f9"),sQuery(id+"F3.wireOp",EDGE,"ce3739ef-15fd-4754-ad9c-ccf511a9a8fb"),sQuery(id+"F3.wireOp",EDGE,"201134a3-66f3-4a3f-aa9b-76948966efc0"),sQuery(id+"F3.wireOp",EDGE,"65b511ea-0759-428d-8070-88e1f521d8ea"),sQuery(id+"F3.wireOp",EDGE,"c37cddb6-5cf8-4891-aff4-7191a72080b9"),sQuery(id+"F3.wireOp",EDGE,"52a43dbd-e952-43e1-be3d-d70e107260e6"),sQuery(id+"F3.wireOp",EDGE,"08c1271f-f5c3-4f26-be27-7f5e21217dff"),sQuery(id+"F3.wireOp",EDGE,"59a09f58-0503-4180-962a-e04db21f0da8"),sQuery(id+"F3.wireOp",EDGE,"e56a4626-e956-42c3-bb5d-cd9dae1ca801"),sQuery(id+"F3.wireOp",EDGE,"5ff5d55f-af90-49eb-8040-353101557de8"),sQuery(id+"F3.wireOp",EDGE,"0ed7430b-e164-4f56-8af9-4534524aa7c0"),sQuery(id+"F3.wireOp",EDGE,"b5610a6e-b6bb-43e3-9a8d-d3d7c5f0098b"),sQuery(id+"F3.wireOp",EDGE,"1d417af8-88ad-47c2-a4e2-6fec82bd6695"),sQuery(id+"F3.wireOp",EDGE,"778ae99a-956a-4ddb-8078-d9bc57f9fc8e"),sQuery(id+"F3.wireOp",EDGE,"5b19af09-f144-446e-9dfa-8766819c9efd"),sQuery(id+"F3.wireOp",EDGE,"028339f6-0475-4a57-af8d-550e32ad7466"),sQuery(id+"F3.wireOp",EDGE,"d5ae35b6-d210-433a-92c8-e92622696872"),sQuery(id+"F3.wireOp",EDGE,"16a2e606-2caa-4876-9ffa-8f08c4ff3a37"),sQuery(id+"F3.wireOp",EDGE,"5b90b144-be56-4de7-a9dd-c1e0336acbe3"),sQuery(id+"F3.wireOp",EDGE,"5912d126-c5fc-41e4-bfb8-b4fefc52ca72"),sQuery(id+"F3.wireOp",EDGE,"2e96ce95-bd3e-4f27-a7f8-b62cf5efe954"),sQuery(id+"F3.wireOp",EDGE,"ecb4e259-1207-4dd0-bc3c-87c6506cc3a5"),sQuery(id+"F3.wireOp",EDGE,"105fb72e-4d79-4204-af2f-b3b26f5eb8d1"),sQuery(id+"F3.wireOp",EDGE,"fa59b598-df54-48c6-bb8f-c5f7618c69d0"),sQuery(id+"F3.wireOp",EDGE,"a6beef0d-f124-47ac-b957-e6cd3057a354"),sQuery(id+"F3.wireOp",EDGE,"7c3eaf53-dcb7-43b1-ad18-80ff953eb59e"),sQuery(id+"F3.wireOp",EDGE,"281fe206-104f-408f-94b6-be79f12604c9")])]});
            var Q1;
            Q1=makeQuery(id+"F4.opExtrude","SWEPT_BODY",BODY,{"disambiguationData":[OSD([sQuery(id+"F3.wireOp",EDGE,"58f6206a-5554-41d4-8cf7-6e0b4724a469"),sQuery(id+"F3.wireOp",EDGE,"85dabe77-b6aa-43d5-a519-64383616f71e"),sQuery(id+"F3.wireOp",EDGE,"4b679fe6-9e11-497d-b8fd-14ca14e49ddd"),sQuery(id+"F3.wireOp",EDGE,"51de25f6-d59e-4805-a327-1fd7e38869c8"),sQuery(id+"F3.wireOp",EDGE,"d47977fb-70d3-4df8-bc35-66fcc0e556e0"),sQuery(id+"F3.wireOp",EDGE,"235006b0-8f14-4ca2-82f0-f96b6b8c4766"),sQuery(id+"F3.wireOp",EDGE,"0fc7acd6-1c1d-47a8-ba12-62eb658d35ca"),sQuery(id+"F3.wireOp",EDGE,"883fa5e3-ca4c-4ce6-a249-4debf538fe24"),sQuery(id+"F3.wireOp",EDGE,"1da09ed1-22d9-43a1-a655-8acff5d61309"),sQuery(id+"F3.wireOp",EDGE,"32654a82-a09a-444f-bf73-45f818f0f235"),sQuery(id+"F3.wireOp",EDGE,"a398fd80-a0a9-4724-ba0e-1a7a000baa92"),sQuery(id+"F3.wireOp",EDGE,"f39f97c8-53f5-4046-9905-b28daecd4f10"),sQuery(id+"F3.wireOp",EDGE,"2484d883-0ec2-4c7d-9023-165ebbef226c"),sQuery(id+"F3.wireOp",EDGE,"f026d96f-3d32-4113-a1c9-3545f5cdbe4a"),sQuery(id+"F3.wireOp",EDGE,"974fee18-719e-4620-aace-d3676da2011b"),sQuery(id+"F3.wireOp",EDGE,"0c5766d2-a026-45af-bffd-0d1f783d5157"),sQuery(id+"F3.wireOp",EDGE,"5da13fee-9c04-45d8-805f-c7a03dde2383"),sQuery(id+"F3.wireOp",EDGE,"dbea32a3-85bd-4957-aef2-b6fe64a02f6b"),sQuery(id+"F3.wireOp",EDGE,"fba134ea-bf40-4191-ad8f-cc6b2b040a97"),sQuery(id+"F3.wireOp",EDGE,"0c19e200-7cd5-4fcb-83ed-261bd7936bc7"),sQuery(id+"F3.wireOp",EDGE,"246b843b-ea86-44e5-9cb9-335e6677b61d"),sQuery(id+"F3.wireOp",EDGE,"c1b3c9bc-1eb4-4c9b-99c8-0cebed89395a"),sQuery(id+"F3.wireOp",EDGE,"f93eebc3-1447-4029-8362-91325193ac2b"),sQuery(id+"F3.wireOp",EDGE,"bf86b12d-53a9-4c19-abaa-b1e658933ceb"),sQuery(id+"F3.wireOp",EDGE,"89646a71-1a60-4e14-b80a-74fb601d0855"),sQuery(id+"F3.wireOp",EDGE,"7b03dcde-0a52-4f3c-80e9-110d1d805e93"),sQuery(id+"F3.wireOp",EDGE,"83e8d1f3-8820-485b-8b6d-3ecd79124883"),sQuery(id+"F3.wireOp",EDGE,"ec7b56eb-ca95-44fd-a774-e9b7f9d3f50d"),sQuery(id+"F3.wireOp",EDGE,"31861aa6-cfd1-43ce-a7c5-bacfb7e2a30f"),sQuery(id+"F3.wireOp",EDGE,"fa3de647-1dd9-4141-982b-74ae8d07851d"),sQuery(id+"F3.wireOp",EDGE,"75d7c1c5-761c-4178-bfd4-4f469045899b"),sQuery(id+"F3.wireOp",EDGE,"4b3d7518-bd5d-4ecc-b2c5-d8dd665de4f4"),sQuery(id+"F3.wireOp",EDGE,"3be2682d-01bd-4f31-9cde-9df16a01e4a9"),sQuery(id+"F3.wireOp",EDGE,"72d3c7a9-2794-46eb-9b0d-6c526cc1b9a3"),sQuery(id+"F3.wireOp",EDGE,"0137e336-6b26-4f8d-b9ad-47ce1aa9eb31"),sQuery(id+"F3.wireOp",EDGE,"96000e4a-2d86-4b9f-af7d-a1c875cc048c"),sQuery(id+"F3.wireOp",EDGE,"139c5a79-9c0f-4e15-b57f-4c09662495a3"),sQuery(id+"F3.wireOp",EDGE,"8ea04d8b-b3da-46bb-9742-d8cba6b23bda"),sQuery(id+"F3.wireOp",EDGE,"b352b580-467e-481c-88ac-6217b8462947"),sQuery(id+"F3.wireOp",EDGE,"2503a493-1722-4539-8d54-7329fc0b116a"),sQuery(id+"F3.wireOp",EDGE,"a0615e06-0a48-4c65-8818-f0f693937022"),sQuery(id+"F3.wireOp",EDGE,"08389002-1ce8-438a-b5a4-698ca33590c2"),sQuery(id+"F3.wireOp",EDGE,"1756e4aa-c30a-461e-962c-81ee35d31e55"),sQuery(id+"F3.wireOp",EDGE,"5f84c249-07ea-4efb-9be3-ca494937f772"),sQuery(id+"F3.wireOp",EDGE,"cbefd041-b54f-4587-87b6-437b2290d1fc"),sQuery(id+"F3.wireOp",EDGE,"d44f58d4-f1a7-4aec-b016-8e7f1e498aeb"),sQuery(id+"F3.wireOp",EDGE,"0a5be90b-7545-44ea-9f2d-c726a5a2121c"),sQuery(id+"F3.wireOp",EDGE,"0cfaa442-d102-4580-8ef6-489f2aa1e6b3")])]});
            var Q2;
            Q2=makeQuery(id+"F4.opExtrude","SWEPT_BODY",BODY,{"disambiguationData":[OSD([sQuery(id+"F3.wireOp",EDGE,"9cc7aec6-4d94-4577-ab6c-32f5aa316238"),sQuery(id+"F3.wireOp",EDGE,"5ab2d840-4a32-405a-8c4b-a8126e3e1bc1"),sQuery(id+"F3.wireOp",EDGE,"56de48b4-9620-4637-8196-310e2641530f"),sQuery(id+"F3.wireOp",EDGE,"55327826-e64b-4830-85f2-3f22d36f43b5"),sQuery(id+"F3.wireOp",EDGE,"0245b46f-a639-4a95-8ca3-1568736ceed2"),sQuery(id+"F3.wireOp",EDGE,"9bd8a002-6ca7-4c84-8984-a620eefad103"),sQuery(id+"F3.wireOp",EDGE,"d4736c5e-da0b-46a0-ba9d-17ae07bb2b66"),sQuery(id+"F3.wireOp",EDGE,"125695b8-77e6-4e99-8f78-5f8fae1a0c71"),sQuery(id+"F3.wireOp",EDGE,"c9f25b10-a495-4684-8f25-8f255fabab6e"),sQuery(id+"F3.wireOp",EDGE,"0dbee67a-2ab6-4abb-ae16-0fe64d623848"),sQuery(id+"F3.wireOp",EDGE,"92c08d8e-ed2e-41a3-9c1a-b5ddaf8a0bf1"),sQuery(id+"F3.wireOp",EDGE,"00fabb15-0c1e-492e-85c1-17390e5b12bc"),sQuery(id+"F3.wireOp",EDGE,"065a9352-dddb-4e3f-b02a-444c867b75fe"),sQuery(id+"F3.wireOp",EDGE,"ef206bb6-e4f2-4189-9fc7-a7823c329ad6"),sQuery(id+"F3.wireOp",EDGE,"7199cbbe-c9bf-4cb9-b928-2ff8a84eb09e"),sQuery(id+"F3.wireOp",EDGE,"17bf9ed1-b881-4f74-816d-3511b6b328c7"),sQuery(id+"F3.wireOp",EDGE,"e5b615d0-4193-495d-b285-bd69ae30f000"),sQuery(id+"F3.wireOp",EDGE,"cfeaf62f-6be1-426b-9732-01e1a667be7e"),sQuery(id+"F3.wireOp",EDGE,"ac56344b-5ee6-4fa5-8e47-65b2a4ea3a01"),sQuery(id+"F3.wireOp",EDGE,"45b5fa53-15fd-43a0-91b0-943cc3286fc9")])]});
            var Q3;
            Q3=makeQuery(id+"F4.opExtrude","SWEPT_BODY",BODY,{"disambiguationData":[OSD([sQuery(id+"F3.wireOp",EDGE,"7bdfe37d-9957-4663-8239-5490fd3220d9"),sQuery(id+"F3.wireOp",EDGE,"6a91314f-c002-4565-bbf8-bb9f29165fb8"),sQuery(id+"F3.wireOp",EDGE,"b69f99c7-a6d0-4d1b-8752-9e82ab4c99ec"),sQuery(id+"F3.wireOp",EDGE,"c928f899-12af-4b01-b412-b3b7da3d830f"),sQuery(id+"F3.wireOp",EDGE,"ffa58721-cdd5-406d-be26-d96f7a050df4"),sQuery(id+"F3.wireOp",EDGE,"02fc7fb8-293b-44ff-ab78-63506d0aedb9"),sQuery(id+"F3.wireOp",EDGE,"147fb6cb-2565-4fb5-9280-6afbf9eef36b"),sQuery(id+"F3.wireOp",EDGE,"2cee3704-4124-415a-b391-31af1cf305d7"),sQuery(id+"F3.wireOp",EDGE,"32b2fb71-03c8-4978-9d95-2b5aaf044d0d"),sQuery(id+"F3.wireOp",EDGE,"e5d05796-7d6c-4350-8a4e-d55f5ade2f77"),sQuery(id+"F3.wireOp",EDGE,"77b1164c-8dd4-4680-b616-ac151a422eb2"),sQuery(id+"F3.wireOp",EDGE,"ec0798b8-0fbb-49ea-9766-39d2ee0936b0"),sQuery(id+"F3.wireOp",EDGE,"c4af6478-2a03-47a6-862f-c0c71886b8a3"),sQuery(id+"F3.wireOp",EDGE,"1912a38f-fa28-45c6-ab33-84cac2787056"),sQuery(id+"F3.wireOp",EDGE,"5d79fa95-f66d-4d2b-923b-4d54735f1fbd"),sQuery(id+"F3.wireOp",EDGE,"2db7aef4-a710-4bcf-9c1c-a8a87719953d"),sQuery(id+"F3.wireOp",EDGE,"183449de-345c-4115-9bca-43a403e62dbd"),sQuery(id+"F3.wireOp",EDGE,"e3ac8c9b-cab5-44b0-ad81-0e2b680c384a"),sQuery(id+"F3.wireOp",EDGE,"92e85db6-f458-41f6-a9a1-1e1a1a7e7809"),sQuery(id+"F3.wireOp",EDGE,"f0dbb46f-43a9-447b-9c75-8dfc9b95470d"),sQuery(id+"F3.wireOp",EDGE,"4b73f5f6-f769-4414-bdba-7d253e58fff4"),sQuery(id+"F3.wireOp",EDGE,"a88669dc-35b3-46bb-964f-c9bf6c4ab898"),sQuery(id+"F3.wireOp",EDGE,"2c559bae-f38f-4377-91e6-3c9de70acf11"),sQuery(id+"F3.wireOp",EDGE,"c1caf99b-adaa-42fe-a319-8cbcd819cf89"),sQuery(id+"F3.wireOp",EDGE,"54b04dd4-0ec4-4956-b19c-1141095738e3"),sQuery(id+"F3.wireOp",EDGE,"098f7a84-b7b8-4879-b21a-5c38879e4110"),sQuery(id+"F3.wireOp",EDGE,"b406a8e6-a226-4f3d-ac30-e4d06e4dac62"),sQuery(id+"F3.wireOp",EDGE,"36f95d1d-68ce-4231-ad71-3960c85e5915"),sQuery(id+"F3.wireOp",EDGE,"dc12cad8-2eed-454e-aa74-30099b1c9064"),sQuery(id+"F3.wireOp",EDGE,"4c78a4fd-cd81-43d6-85d6-6e4d3fbc1e98"),sQuery(id+"F3.wireOp",EDGE,"ee9e30de-787b-4e8f-b425-43a8e9289f81"),sQuery(id+"F3.wireOp",EDGE,"2518a3a4-c96b-4463-8704-0b71c65c60d2"),sQuery(id+"F3.wireOp",EDGE,"c9129a67-398c-4e37-92cb-2d54ff2e2e82"),sQuery(id+"F3.wireOp",EDGE,"d429d547-9f5b-42c6-bcca-effad2fa908f"),sQuery(id+"F3.wireOp",EDGE,"99d16e94-b2b3-43d5-9c7b-7bd463994dcb"),sQuery(id+"F3.wireOp",EDGE,"32993909-9a70-47ee-9097-89fff220f839"),sQuery(id+"F3.wireOp",EDGE,"6eabbeed-9496-4825-b168-63782a34f495"),sQuery(id+"F3.wireOp",EDGE,"f74987e3-8e60-4a5b-857f-839ae8aaf0cf"),sQuery(id+"F3.wireOp",EDGE,"1c218c86-035d-4441-93c0-9621d3297c3a"),sQuery(id+"F3.wireOp",EDGE,"0133f513-4b11-4cc4-b075-4625e9591e41"),sQuery(id+"F3.wireOp",EDGE,"fe921ad4-a8f5-4772-9aeb-350aca2e8948"),sQuery(id+"F3.wireOp",EDGE,"bfde0a4f-3cec-4f8e-8a23-dd1441b34c2b"),sQuery(id+"F3.wireOp",EDGE,"b41521ff-c5df-4b64-83ed-5e7635cf4438"),sQuery(id+"F3.wireOp",EDGE,"ed692599-6bbb-4379-8e89-ea326a0a0f87"),sQuery(id+"F3.wireOp",EDGE,"a98451c0-d76c-436e-99f9-a3fe9c8430a4"),sQuery(id+"F3.wireOp",EDGE,"561965b2-3050-4f49-9305-d98a2b852bbe"),sQuery(id+"F3.wireOp",EDGE,"e13dfa59-48e6-4b4e-94b9-1fc5254b0f2e"),sQuery(id+"F3.wireOp",EDGE,"0354e106-253a-4bfa-b5b7-b09cd0f2f6c0"),sQuery(id+"F3.wireOp",EDGE,"8df1dcc8-d00a-4777-85fd-8af8e9830bd1"),sQuery(id+"F3.wireOp",EDGE,"26ce3762-0d1a-4b81-9a23-debcfc24da1c"),sQuery(id+"F3.wireOp",EDGE,"3e900f8f-3ffb-4e32-b536-61fea2f3e30a"),sQuery(id+"F3.wireOp",EDGE,"4a1b5445-5559-461f-b6f1-b4cd9b95ea10")])]});
            var Q4;
            Q4=makeQuery(id+"F1.opRevolve","SWEPT_BODY",BODY,{"disambiguationData":[OSD([sQuery(id+"F0.wireOp",EDGE,"E0"),sQuery(id+"F0.wireOp",EDGE,"E1")])]});
            var Q5;
            Q5=qCreatedBy(makeId("Origin.pointOp"),VERTEX);
            transform(context, id + "F5", {"entities" : qUnion([Q0, Q1, Q2, Q3, Q4]), "transformType" : TransformType.SCALE_UNIFORMLY, "scale" : 0.03, "scalePoint" : qUnion([Q5]), "makeCopy" : false});
        }
        {
            var Q0;
            Q0=qCreatedBy(makeId("Top.planeOp"),FACE);
            var sketch = newSketch(context, id + "F6", { "sketchPlane" : qUnion([Q0])});
            skLineSegment(sketch, "E314", {"start": v(0, 15) * mm, "end": v(0, -15) * mm});
            skArc(sketch, "E315", {"start": v(0, 15) * mm, "mid": v(-15, 0) * mm, "end": v(0, -15) * mm});
            skArc(sketch, "E316", {"start": v(0, 10.25) * mm, "mid": v(-10.25, 0) * mm, "end": v(0, -10.25) * mm});
            skArc(sketch, "E317", {"start": v(0, 7) * mm, "mid": v(-7, 0) * mm, "end": v(0, -7) * mm});
            skSolve(sketch);
        }
        {
            var Q0;
            {var subQ0=sQuery(id+"F6.wireOp",EDGE,"E315");Q0=makeQuery(id+"F6.imprint","IMPRINT",FACE,{"disambiguationData":[TD([[makeQuery(id+"F6.imprint","IMPRINT",EDGE,{"derivedFrom":subQ0}),1.0]])]});}
            var Q1;
            {var subQ0=sQuery(id+"F6.wireOp",EDGE,"E317");Q1=makeQuery(id+"F6.imprint","IMPRINT",FACE,{"disambiguationData":[TD([[makeQuery(id+"F6.imprint","IMPRINT",EDGE,{"derivedFrom":subQ0}),1.0]])]});}
            var Q2;
            Q2=sQuery(id+"F6.wireOp",EDGE,"E314");
            revolve(context, id + "F7", {"operationType" : NewBodyOperationType.REMOVE, "entities" : qUnion([Q0, Q1]), "axis" : qUnion([Q2]), "revolveType" : RevolveType.FULL});
        }
        {
            var Q0;
            Q0=makeQuery(id+"F1.opRevolve","SWEPT_BODY",BODY,{"disambiguationData":[OSD([sQuery(id+"F0.wireOp",EDGE,"E0"),sQuery(id+"F0.wireOp",EDGE,"E1")])]});
            var Q1;
            Q1=sQuery(id+"F0.wireOp",VERTEX,"E1.center");
            transform(context, id + "F8", {"entities" : qUnion([Q0]), "transformType" : TransformType.SCALE_UNIFORMLY, "scale" : 1.4, "scalePoint" : qUnion([Q1]), "makeCopy" : false});
        }
        {
            var Q0;
            Q0=qCreatedBy(makeId("Front.planeOp"),FACE);
            var sketch = newSketch(context, id + "F9", { "sketchPlane" : qUnion([Q0])});
            skCircle(sketch, "E318", {"center": v(0, -5.12) * mm, "radius": 2 * mm});
            skSolve(sketch);
        }
        {
            var Q0;
            Q0=qSketchRegion(id+"F9",true);
            extrude(context, id + "F10", {"entities" : qUnion([Q0]), "operationType" : NewBodyOperationType.REMOVE, "oppositeDirection" : true, "depth" : 25 * mm});
        }
        {
            var Q0;
            Q0=qCreatedBy(makeId("Top.planeOp"),FACE);
            var sketch = newSketch(context, id + "F11", { "sketchPlane" : qUnion([Q0])});
            skLineSegment(sketch, "E319", {"start": v(-23.6, 0) * mm, "end": v(33.49, 0) * mm});
            skArc(sketch, "E320", {"start": v(-14.25, 0) * mm, "mid": v(0, 14.25) * mm, "end": v(14.25, 0) * mm});
            skSolve(sketch);
        }
        {
            var Q0;
            Q0=sQuery(id+"F11.wireOp",EDGE,"E319");
            cPlane(context, id + "F12", {"entities" : qUnion([Q0]), "cplaneType" : CPlaneType.LINE_ANGLE, "offset" : 25 * mm, "angle" : 40 * degree, "width" : 150 * mm, "height" : 150 * mm});
        }
        {
            var Q0;
            Q0=qCreatedBy(id+"F12.planeOp",FACE);
            var sketch = newSketch(context, id + "F13", { "sketchPlane" : qUnion([Q0])});
            skText(sketch, "E321", { "text": "intent", "fontName": "OpenSans-Italic.ttf"});
            const initialGuessF13  = {"E321": [-0.00735, -0.003, 1, 0, 0.004]};
            skSetInitialGuess(sketch, initialGuessF13);
            skSolve(sketch);
        }
        {
            var Q0;
            Q0=sQuery(id+"F11.wireOp",EDGE,"E320");
            var Q1;
            Q1=sQuery(id+"F11.wireOp",EDGE,"E319");
            revolve(context, id + "F14", {"bodyType" : ToolBodyType.SURFACE, "surfaceEntities" : qUnion([Q0]), "axis" : qUnion([Q1]), "revolveType" : RevolveType.FULL});
        }
        {
            var Q0;
            Q0 = qSketchRegion(id + "F13", true);
            var Q1;
            Q1=makeQuery(id+"F14.opRevolve","SWEPT_FACE",FACE,{"disambiguationData":[OSD([sQuery(id+"F11.wireOp",EDGE,"E320")])]});
            extrude(context, id + "F15", {"entities" : qUnion([Q0]), "operationType" : NewBodyOperationType.ADD, "endBound" : BoundingType.UP_TO_SURFACE, "depth" : 25 * mm, "endBoundEntityFace" : qUnion([Q1]), "offsetDistance" : 25 * mm});
        }
    });
